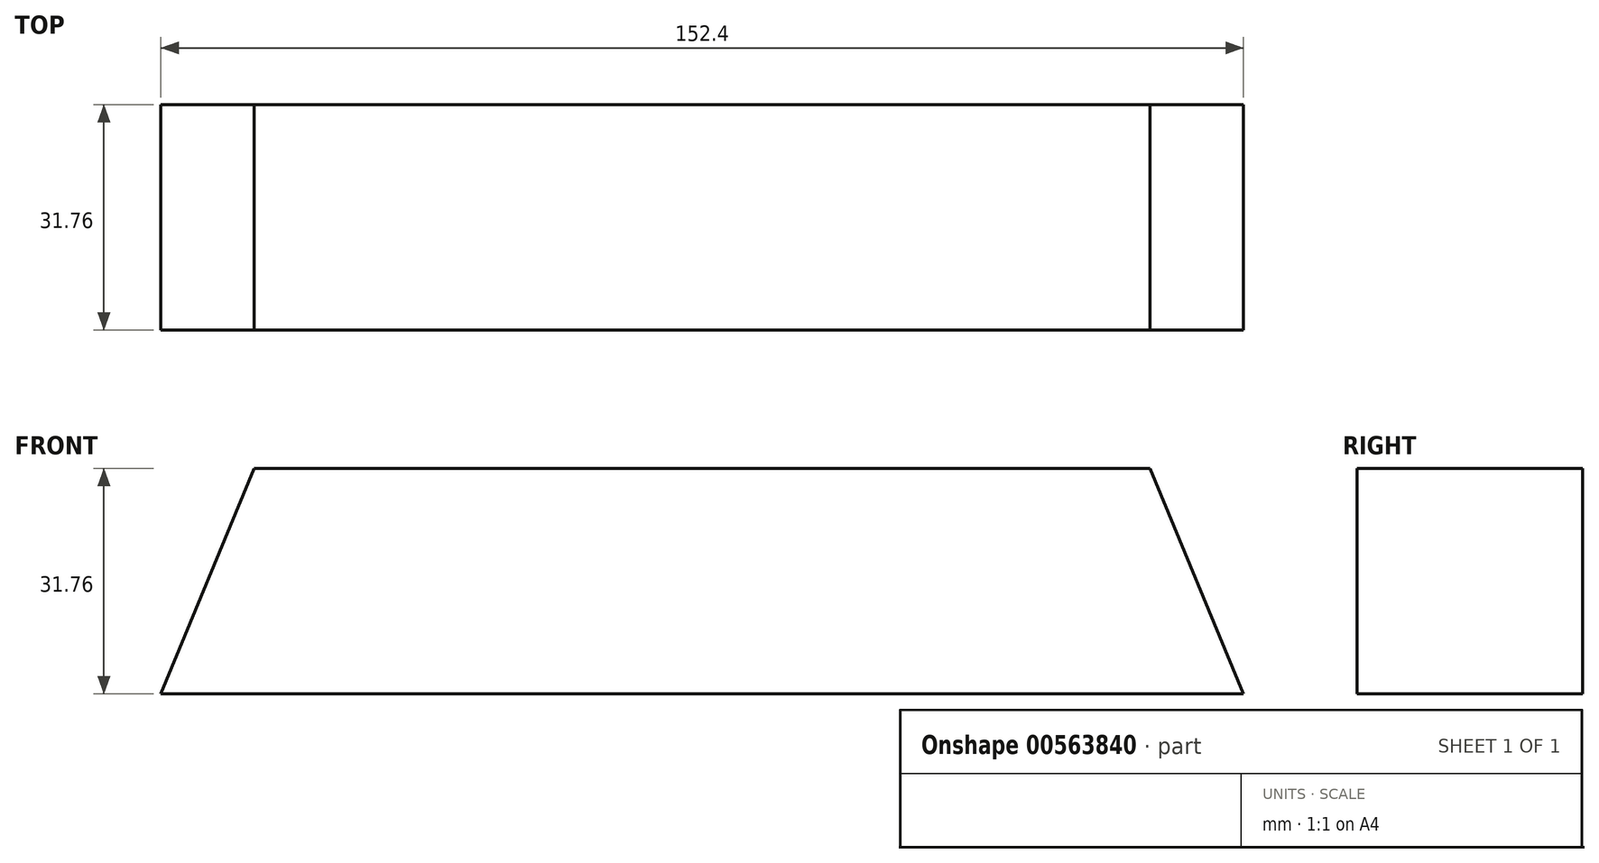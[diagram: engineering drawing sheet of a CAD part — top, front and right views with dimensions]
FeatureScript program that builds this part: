
annotation { "Feature Type Name" : "Feature", "Feature Type Description" : "" }
export const myFeature = defineFeature(function(context is Context, id is Id, definition is map)
    precondition{}
    {
        {
            var Q0;
            Q0=qCreatedBy(makeId("Front.planeOp"),FACE);
            var sketch = newSketch(context, id + "F0", { "sketchPlane" : qUnion([Q0])});
            skLineSegment(sketch, "E0.bottom", {"start": v(-76.2, 15.88) * mm, "end": v(76.2, 15.88) * mm});
            skLineSegment(sketch, "E0.top", {"start": v(-76.2, -15.88) * mm, "end": v(76.2, -15.88) * mm});
            skLineSegment(sketch, "E0.left", {"start": v(-76.2, 15.88) * mm, "end": v(-76.2, -15.88) * mm});
            skLineSegment(sketch, "E0.right", {"start": v(76.2, 15.88) * mm, "end": v(76.2, -15.88) * mm});
            skPoint(sketch, "E0.middle", {"position": v(0, 0) * mm});
            skLineSegment(sketch, "E1", {"start": v(-76.2, -15.88) * mm, "end": v(-63.05, 15.88) * mm});
            skLineSegment(sketch, "E2", {"start": v(76.2, -15.88) * mm, "end": v(63.05, 15.87) * mm});
            skSolve(sketch);
        }
        {
            var Q0;
            Q0=makeQuery(id+"F0.imprint","IMPRINT",FACE,{"disambiguationData":[TD([[makeQuery(id+"F0.imprint","IMPRINT",EDGE,{"derivedFrom":sQuery(id+"F0.wireOp",EDGE,"E0.top")}),1.0]])]});
            extrude(context, id + "F1", {"entities" : qUnion([Q0]), "endBound" : BoundingType.SYMMETRIC, "depth" : 31.75 * mm, "offsetDistance" : 25.4 * mm});
        }
    });
